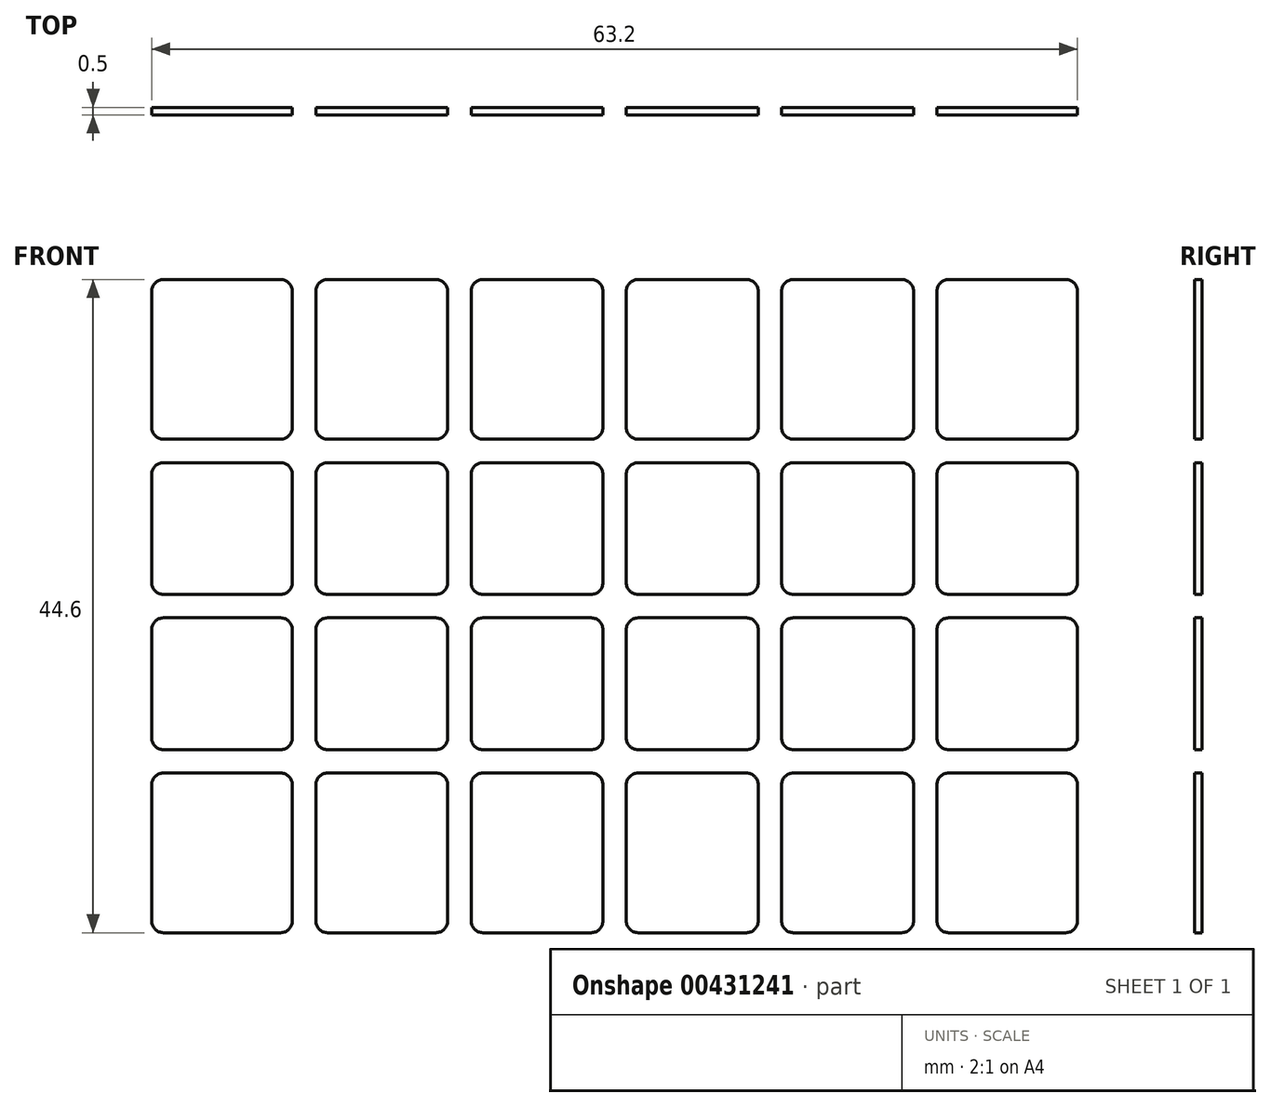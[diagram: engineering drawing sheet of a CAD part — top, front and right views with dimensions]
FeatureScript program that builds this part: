
annotation { "Feature Type Name" : "Feature", "Feature Type Description" : "" }
export const myFeature = defineFeature(function(context is Context, id is Id, definition is map)
    precondition{}
    {
        {
            var Q0;
            Q0=qCreatedBy(makeId("Front.planeOp"),FACE);
            var sketch = newSketch(context, id + "F0", { "sketchPlane" : qUnion([Q0])});
            skLineSegment(sketch, "E0.bottom", {"start": v(0.8, 0) * mm, "end": v(8.8, 0) * mm});
            skLineSegment(sketch, "E0.top", {"start": v(0.8, 9) * mm, "end": v(8.8, 9) * mm});
            skLineSegment(sketch, "E0.left", {"start": v(0, 0.8) * mm, "end": v(0, 8.2) * mm});
            skLineSegment(sketch, "E0.right", {"start": v(9.6, 0.8) * mm, "end": v(9.6, 8.2) * mm});
            skPoint(sketch, "E1.visualSharp", {"position": v(0, 9) * mm});
            skArc(sketch, "E1.filletArc", {"start": v(0.8, 9) * mm, "mid": v(0.23, 8.77) * mm, "end": v(0, 8.2) * mm});
            skPoint(sketch, "E2.visualSharp", {"position": v(9.6, 9) * mm});
            skArc(sketch, "E2.filletArc", {"start": v(9.6, 8.2) * mm, "mid": v(9.37, 8.77) * mm, "end": v(8.8, 9) * mm});
            skPoint(sketch, "E3.visualSharp", {"position": v(9.6, 0) * mm});
            skArc(sketch, "E3.filletArc", {"start": v(8.8, 0) * mm, "mid": v(9.37, 0.23) * mm, "end": v(9.6, 0.8) * mm});
            skPoint(sketch, "E4.visualSharp", {"position": v(0, 0) * mm});
            skArc(sketch, "E4.filletArc", {"start": v(0, 0.8) * mm, "mid": v(0.23, 0.23) * mm, "end": v(0.8, 0) * mm});
            skLineSegment(sketch, "E5.bottom", {"start": v(12, 0) * mm, "end": v(19.4, 0) * mm});
            skLineSegment(sketch, "E5.top", {"start": v(12, 9) * mm, "end": v(19.4, 9) * mm});
            skLineSegment(sketch, "E5.left", {"start": v(11.2, 0.8) * mm, "end": v(11.2, 8.2) * mm});
            skLineSegment(sketch, "E5.right", {"start": v(20.2, 0.8) * mm, "end": v(20.2, 8.2) * mm});
            skPoint(sketch, "E6.visualSharp", {"position": v(11.2, 9) * mm});
            skArc(sketch, "E6.filletArc", {"start": v(12, 9) * mm, "mid": v(11.43, 8.77) * mm, "end": v(11.2, 8.2) * mm});
            skPoint(sketch, "E7.visualSharp", {"position": v(20.2, 9) * mm});
            skArc(sketch, "E7.filletArc", {"start": v(20.2, 8.2) * mm, "mid": v(19.97, 8.77) * mm, "end": v(19.4, 9) * mm});
            skPoint(sketch, "E8.visualSharp", {"position": v(20.2, 0) * mm});
            skArc(sketch, "E8.filletArc", {"start": v(19.4, 0) * mm, "mid": v(19.97, 0.23) * mm, "end": v(20.2, 0.8) * mm});
            skPoint(sketch, "E9.visualSharp", {"position": v(11.2, 0) * mm});
            skArc(sketch, "E9.filletArc", {"start": v(11.2, 0.8) * mm, "mid": v(11.43, 0.23) * mm, "end": v(12, 0) * mm});
            skLineSegment(sketch, "E10.1.0.0", {"start": v(22.6, 9) * mm, "end": v(30, 9) * mm});
            skLineSegment(sketch, "E10.1.0.1", {"start": v(22.6, 0) * mm, "end": v(30, 0) * mm});
            skLineSegment(sketch, "E10.1.0.2", {"start": v(21.8, 0.8) * mm, "end": v(21.8, 8.2) * mm});
            skPoint(sketch, "E10.1.0.3", {"position": v(21.8, 9) * mm});
            skPoint(sketch, "E10.1.0.4", {"position": v(30.8, 9) * mm});
            skLineSegment(sketch, "E10.1.0.5", {"start": v(30.8, 0.8) * mm, "end": v(30.8, 8.2) * mm});
            skPoint(sketch, "E10.1.0.6", {"position": v(21.8, 0) * mm});
            skPoint(sketch, "E10.1.0.7", {"position": v(30.8, 0) * mm});
            skArc(sketch, "E10.1.0.8", {"start": v(30.8, 8.2) * mm, "mid": v(30.57, 8.77) * mm, "end": v(30, 9) * mm});
            skArc(sketch, "E10.1.0.9", {"start": v(21.8, 0.8) * mm, "mid": v(22.03, 0.23) * mm, "end": v(22.6, 0) * mm});
            skArc(sketch, "E10.1.0.10", {"start": v(30, 0) * mm, "mid": v(30.57, 0.23) * mm, "end": v(30.8, 0.8) * mm});
            skArc(sketch, "E10.1.0.11", {"start": v(22.6, 9) * mm, "mid": v(22.03, 8.77) * mm, "end": v(21.8, 8.2) * mm});
            skLineSegment(sketch, "E10.2.0.0", {"start": v(33.2, 9) * mm, "end": v(40.6, 9) * mm});
            skLineSegment(sketch, "E10.2.0.1", {"start": v(33.2, 0) * mm, "end": v(40.6, 0) * mm});
            skLineSegment(sketch, "E10.2.0.2", {"start": v(32.4, 0.8) * mm, "end": v(32.4, 8.2) * mm});
            skPoint(sketch, "E10.2.0.3", {"position": v(32.4, 9) * mm});
            skPoint(sketch, "E10.2.0.4", {"position": v(41.4, 9) * mm});
            skLineSegment(sketch, "E10.2.0.5", {"start": v(41.4, 0.8) * mm, "end": v(41.4, 8.2) * mm});
            skPoint(sketch, "E10.2.0.6", {"position": v(32.4, 0) * mm});
            skPoint(sketch, "E10.2.0.7", {"position": v(41.4, 0) * mm});
            skArc(sketch, "E10.2.0.8", {"start": v(41.4, 8.2) * mm, "mid": v(41.17, 8.77) * mm, "end": v(40.6, 9) * mm});
            skArc(sketch, "E10.2.0.9", {"start": v(32.4, 0.8) * mm, "mid": v(32.63, 0.23) * mm, "end": v(33.2, 0) * mm});
            skArc(sketch, "E10.2.0.10", {"start": v(40.6, 0) * mm, "mid": v(41.17, 0.23) * mm, "end": v(41.4, 0.8) * mm});
            skArc(sketch, "E10.2.0.11", {"start": v(33.2, 9) * mm, "mid": v(32.63, 8.77) * mm, "end": v(32.4, 8.2) * mm});
            skLineSegment(sketch, "E10.3.0.0", {"start": v(43.8, 9) * mm, "end": v(51.2, 9) * mm});
            skLineSegment(sketch, "E10.3.0.1", {"start": v(43.8, 0) * mm, "end": v(51.2, 0) * mm});
            skLineSegment(sketch, "E10.3.0.2", {"start": v(43, 0.8) * mm, "end": v(43, 8.2) * mm});
            skPoint(sketch, "E10.3.0.3", {"position": v(43, 9) * mm});
            skPoint(sketch, "E10.3.0.4", {"position": v(52, 9) * mm});
            skLineSegment(sketch, "E10.3.0.5", {"start": v(52, 0.8) * mm, "end": v(52, 8.2) * mm});
            skPoint(sketch, "E10.3.0.6", {"position": v(43, 0) * mm});
            skPoint(sketch, "E10.3.0.7", {"position": v(52, 0) * mm});
            skArc(sketch, "E10.3.0.8", {"start": v(52, 8.2) * mm, "mid": v(51.77, 8.77) * mm, "end": v(51.2, 9) * mm});
            skArc(sketch, "E10.3.0.9", {"start": v(43, 0.8) * mm, "mid": v(43.23, 0.23) * mm, "end": v(43.8, 0) * mm});
            skArc(sketch, "E10.3.0.10", {"start": v(51.2, 0) * mm, "mid": v(51.77, 0.23) * mm, "end": v(52, 0.8) * mm});
            skArc(sketch, "E10.3.0.11", {"start": v(43.8, 9) * mm, "mid": v(43.23, 8.77) * mm, "end": v(43, 8.2) * mm});
            skLineSegment(sketch, "E10.direction1", {"start": v(11.2, 0) * mm, "end": v(21.8, 0) * mm, "construction": true});
            skLineSegment(sketch, "E11", {"start": v(30.8, 9) * mm, "end": v(32.4, 9) * mm, "construction": true});
            skLineSegment(sketch, "E12", {"start": v(30.8, 0) * mm, "end": v(32.4, 0) * mm, "construction": true});
            skLineSegment(sketch, "E13", {"start": v(31.6, 9) * mm, "end": v(31.6, 0) * mm, "construction": true});
            skArc(sketch, "E14.MirrorCS", {"start": v(54.4, 0) * mm, "mid": v(53.83, 0.23) * mm, "end": v(53.6, 0.8) * mm});
            skArc(sketch, "E15.MirrorCS", {"start": v(62.4, 9) * mm, "mid": v(62.97, 8.77) * mm, "end": v(63.2, 8.2) * mm});
            skArc(sketch, "E16.MirrorCS", {"start": v(63.2, 0.8) * mm, "mid": v(62.97, 0.23) * mm, "end": v(62.4, 0) * mm});
            skArc(sketch, "E17.MirrorCS", {"start": v(53.6, 8.2) * mm, "mid": v(53.83, 8.77) * mm, "end": v(54.4, 9) * mm});
            skLineSegment(sketch, "E18.MirrorCS", {"start": v(62.4, 9) * mm, "end": v(54.4, 9) * mm});
            skLineSegment(sketch, "E19.MirrorCS", {"start": v(63.2, 0.8) * mm, "end": v(63.2, 8.2) * mm});
            skPoint(sketch, "E20.MirrorP", {"position": v(53.6, 9) * mm});
            skLineSegment(sketch, "E21.MirrorCS", {"start": v(62.4, 0) * mm, "end": v(54.4, 0) * mm});
            skPoint(sketch, "E22.MirrorP", {"position": v(63.2, 9) * mm});
            skLineSegment(sketch, "E23.MirrorCS", {"start": v(53.6, 0.8) * mm, "end": v(53.6, 8.2) * mm});
            skPoint(sketch, "E24.MirrorP", {"position": v(63.2, 0) * mm});
            skPoint(sketch, "E25.MirrorP", {"position": v(53.6, 0) * mm});
            skLineSegment(sketch, "E26", {"start": v(14.28, 9.8) * mm, "end": v(38.56, 9.8) * mm, "construction": true});
            skArc(sketch, "E27.MirrorCS", {"start": v(33.2, 10.6) * mm, "mid": v(32.63, 10.83) * mm, "end": v(32.4, 11.4) * mm});
            skArc(sketch, "E28.MirrorCS", {"start": v(20.2, 11.4) * mm, "mid": v(19.97, 10.83) * mm, "end": v(19.4, 10.6) * mm});
            skArc(sketch, "E29.MirrorCS", {"start": v(52, 11.4) * mm, "mid": v(51.77, 10.83) * mm, "end": v(51.2, 10.6) * mm});
            skArc(sketch, "E30.MirrorCS", {"start": v(19.4, 19.6) * mm, "mid": v(19.97, 19.37) * mm, "end": v(20.2, 18.8) * mm});
            skArc(sketch, "E31.MirrorCS", {"start": v(41.4, 11.4) * mm, "mid": v(41.17, 10.83) * mm, "end": v(40.6, 10.6) * mm});
            skArc(sketch, "E32.MirrorCS", {"start": v(0, 18.8) * mm, "mid": v(0.23, 19.37) * mm, "end": v(0.8, 19.6) * mm});
            skArc(sketch, "E33.MirrorCS", {"start": v(40.6, 19.6) * mm, "mid": v(41.17, 19.37) * mm, "end": v(41.4, 18.8) * mm});
            skArc(sketch, "E34.MirrorCS", {"start": v(43.8, 10.6) * mm, "mid": v(43.23, 10.83) * mm, "end": v(43, 11.4) * mm});
            skArc(sketch, "E35.MirrorCS", {"start": v(12, 10.6) * mm, "mid": v(11.43, 10.83) * mm, "end": v(11.2, 11.4) * mm});
            skArc(sketch, "E36.MirrorCS", {"start": v(53.6, 11.4) * mm, "mid": v(53.83, 10.83) * mm, "end": v(54.4, 10.6) * mm});
            skArc(sketch, "E37.MirrorCS", {"start": v(51.2, 19.6) * mm, "mid": v(51.77, 19.37) * mm, "end": v(52, 18.8) * mm});
            skArc(sketch, "E38.MirrorCS", {"start": v(21.8, 18.8) * mm, "mid": v(22.03, 19.37) * mm, "end": v(22.6, 19.6) * mm});
            skLineSegment(sketch, "E39.MirrorCS", {"start": v(30.8, 19.6) * mm, "end": v(32.4, 19.6) * mm, "construction": true});
            skArc(sketch, "E40.MirrorCS", {"start": v(30.8, 11.4) * mm, "mid": v(30.57, 10.83) * mm, "end": v(30, 10.6) * mm});
            skArc(sketch, "E41.MirrorCS", {"start": v(30, 19.6) * mm, "mid": v(30.57, 19.37) * mm, "end": v(30.8, 18.8) * mm});
            skArc(sketch, "E42.MirrorCS", {"start": v(32.4, 18.8) * mm, "mid": v(32.63, 19.37) * mm, "end": v(33.2, 19.6) * mm});
            skArc(sketch, "E43.MirrorCS", {"start": v(11.2, 18.8) * mm, "mid": v(11.43, 19.37) * mm, "end": v(12, 19.6) * mm});
            skArc(sketch, "E44.MirrorCS", {"start": v(8.8, 19.6) * mm, "mid": v(9.37, 19.37) * mm, "end": v(9.6, 18.8) * mm});
            skArc(sketch, "E45.MirrorCS", {"start": v(43, 18.8) * mm, "mid": v(43.23, 19.37) * mm, "end": v(43.8, 19.6) * mm});
            skArc(sketch, "E46.MirrorCS", {"start": v(22.6, 10.6) * mm, "mid": v(22.03, 10.83) * mm, "end": v(21.8, 11.4) * mm});
            skLineSegment(sketch, "E47.MirrorCS", {"start": v(30.8, 10.6) * mm, "end": v(32.4, 10.6) * mm, "construction": true});
            skArc(sketch, "E48.MirrorCS", {"start": v(54.4, 19.6) * mm, "mid": v(53.83, 19.37) * mm, "end": v(53.6, 18.8) * mm});
            skArc(sketch, "E49.MirrorCS", {"start": v(63.2, 18.8) * mm, "mid": v(62.97, 19.37) * mm, "end": v(62.4, 19.6) * mm});
            skArc(sketch, "E50.MirrorCS", {"start": v(62.4, 10.6) * mm, "mid": v(62.97, 10.83) * mm, "end": v(63.2, 11.4) * mm});
            skArc(sketch, "E51.MirrorCS", {"start": v(0.8, 10.6) * mm, "mid": v(0.23, 10.83) * mm, "end": v(0, 11.4) * mm});
            skArc(sketch, "E52.MirrorCS", {"start": v(9.6, 11.4) * mm, "mid": v(9.37, 10.83) * mm, "end": v(8.8, 10.6) * mm});
            skLineSegment(sketch, "E53.MirrorCS", {"start": v(12, 19.6) * mm, "end": v(19.4, 19.6) * mm});
            skPoint(sketch, "E54.MirrorP", {"position": v(21.8, 10.6) * mm});
            skPoint(sketch, "E55.MirrorP", {"position": v(63.2, 19.6) * mm});
            skLineSegment(sketch, "E56.MirrorCS", {"start": v(62.4, 10.6) * mm, "end": v(54.4, 10.6) * mm});
            skPoint(sketch, "E57.MirrorP", {"position": v(32.4, 10.6) * mm});
            skLineSegment(sketch, "E58.MirrorCS", {"start": v(22.6, 19.6) * mm, "end": v(30, 19.6) * mm});
            skLineSegment(sketch, "E59.MirrorCS", {"start": v(31.6, 10.6) * mm, "end": v(31.6, 19.6) * mm, "construction": true});
            skLineSegment(sketch, "E60.MirrorCS", {"start": v(33.2, 10.6) * mm, "end": v(40.6, 10.6) * mm});
            skPoint(sketch, "E61.MirrorP", {"position": v(20.2, 10.6) * mm});
            skPoint(sketch, "E62.MirrorP", {"position": v(52, 10.6) * mm});
            skPoint(sketch, "E63.MirrorP", {"position": v(43, 19.6) * mm});
            skPoint(sketch, "E64.MirrorP", {"position": v(30.8, 10.6) * mm});
            skLineSegment(sketch, "E65.MirrorCS", {"start": v(52, 18.8) * mm, "end": v(52, 11.4) * mm});
            skLineSegment(sketch, "E66.MirrorCS", {"start": v(11.2, 19.6) * mm, "end": v(21.8, 19.6) * mm, "construction": true});
            skLineSegment(sketch, "E67.MirrorCS", {"start": v(41.4, 18.8) * mm, "end": v(41.4, 11.4) * mm});
            skPoint(sketch, "E68.MirrorP", {"position": v(41.4, 19.6) * mm});
            skPoint(sketch, "E69.MirrorP", {"position": v(53.6, 10.6) * mm});
            skLineSegment(sketch, "E70.MirrorCS", {"start": v(21.8, 18.8) * mm, "end": v(21.8, 11.4) * mm});
            skPoint(sketch, "E71.MirrorP", {"position": v(21.8, 19.6) * mm});
            skLineSegment(sketch, "E72.MirrorCS", {"start": v(62.4, 19.6) * mm, "end": v(54.4, 19.6) * mm});
            skLineSegment(sketch, "E73.MirrorCS", {"start": v(43.8, 10.6) * mm, "end": v(51.2, 10.6) * mm});
            skPoint(sketch, "E74.MirrorP", {"position": v(0, 19.6) * mm});
            skPoint(sketch, "E75.MirrorP", {"position": v(9.6, 19.6) * mm});
            skPoint(sketch, "E76.MirrorP", {"position": v(20.2, 19.6) * mm});
            skPoint(sketch, "E77.MirrorP", {"position": v(32.4, 19.6) * mm});
            skLineSegment(sketch, "E78.MirrorCS", {"start": v(33.2, 19.6) * mm, "end": v(40.6, 19.6) * mm});
            skPoint(sketch, "E79.MirrorP", {"position": v(63.2, 10.6) * mm});
            skLineSegment(sketch, "E80.MirrorCS", {"start": v(22.6, 10.6) * mm, "end": v(30, 10.6) * mm});
            skLineSegment(sketch, "E81.MirrorCS", {"start": v(12, 10.6) * mm, "end": v(19.4, 10.6) * mm});
            skLineSegment(sketch, "E82.MirrorCS", {"start": v(30.8, 18.8) * mm, "end": v(30.8, 11.4) * mm});
            skLineSegment(sketch, "E83.MirrorCS", {"start": v(20.2, 18.8) * mm, "end": v(20.2, 11.4) * mm});
            skPoint(sketch, "E84.MirrorP", {"position": v(53.6, 19.6) * mm});
            skLineSegment(sketch, "E85.MirrorCS", {"start": v(43.8, 19.6) * mm, "end": v(51.2, 19.6) * mm});
            skPoint(sketch, "E86.MirrorP", {"position": v(11.2, 19.6) * mm});
            skLineSegment(sketch, "E87.MirrorCS", {"start": v(43, 18.8) * mm, "end": v(43, 11.4) * mm});
            skLineSegment(sketch, "E88.MirrorCS", {"start": v(53.6, 18.8) * mm, "end": v(53.6, 11.4) * mm});
            skPoint(sketch, "E89.MirrorP", {"position": v(11.2, 10.6) * mm});
            skLineSegment(sketch, "E90.MirrorCS", {"start": v(11.2, 18.8) * mm, "end": v(11.2, 11.4) * mm});
            skLineSegment(sketch, "E91.MirrorCS", {"start": v(63.2, 18.8) * mm, "end": v(63.2, 11.4) * mm});
            skPoint(sketch, "E92.MirrorP", {"position": v(0, 10.6) * mm});
            skPoint(sketch, "E93.MirrorP", {"position": v(30.8, 19.6) * mm});
            skPoint(sketch, "E94.MirrorP", {"position": v(52, 19.6) * mm});
            skPoint(sketch, "E95.MirrorP", {"position": v(43, 10.6) * mm});
            skLineSegment(sketch, "E96.MirrorCS", {"start": v(32.4, 18.8) * mm, "end": v(32.4, 11.4) * mm});
            skPoint(sketch, "E97.MirrorP", {"position": v(41.4, 10.6) * mm});
            skLineSegment(sketch, "E98.MirrorCS", {"start": v(0.8, 19.6) * mm, "end": v(8.8, 19.6) * mm});
            skLineSegment(sketch, "E99.MirrorCS", {"start": v(9.6, 18.8) * mm, "end": v(9.6, 11.4) * mm});
            skPoint(sketch, "E100.MirrorP", {"position": v(9.6, 10.6) * mm});
            skLineSegment(sketch, "E101.MirrorCS", {"start": v(0.8, 10.6) * mm, "end": v(8.8, 10.6) * mm});
            skLineSegment(sketch, "E102.MirrorCS", {"start": v(0, 18.8) * mm, "end": v(0, 11.4) * mm});
            skLineSegment(sketch, "E103.bottom", {"start": v(8.8, 21.2) * mm, "end": v(0.8, 21.2) * mm});
            skLineSegment(sketch, "E103.top", {"start": v(8.8, 32.1) * mm, "end": v(0.8, 32.1) * mm});
            skLineSegment(sketch, "E103.left", {"start": v(9.6, 22) * mm, "end": v(9.6, 31.3) * mm});
            skLineSegment(sketch, "E103.right", {"start": v(0, 22) * mm, "end": v(0, 31.3) * mm});
            skPoint(sketch, "E104.visualSharp", {"position": v(0, 32.1) * mm});
            skArc(sketch, "E104.filletArc", {"start": v(0.8, 32.1) * mm, "mid": v(0.23, 31.87) * mm, "end": v(0, 31.3) * mm});
            skPoint(sketch, "E105.visualSharp", {"position": v(9.6, 32.1) * mm});
            skArc(sketch, "E105.filletArc", {"start": v(9.6, 31.3) * mm, "mid": v(9.37, 31.87) * mm, "end": v(8.8, 32.1) * mm});
            skPoint(sketch, "E106.visualSharp", {"position": v(9.6, 21.2) * mm});
            skArc(sketch, "E106.filletArc", {"start": v(8.8, 21.2) * mm, "mid": v(9.37, 21.43) * mm, "end": v(9.6, 22) * mm});
            skPoint(sketch, "E107.visualSharp", {"position": v(0, 21.2) * mm});
            skArc(sketch, "E107.filletArc", {"start": v(0, 22) * mm, "mid": v(0.23, 21.43) * mm, "end": v(0.8, 21.2) * mm});
            skLineSegment(sketch, "E108.bottom", {"start": v(12, 21.2) * mm, "end": v(19.4, 21.2) * mm});
            skLineSegment(sketch, "E108.top", {"start": v(12, 32.1) * mm, "end": v(19.4, 32.1) * mm});
            skLineSegment(sketch, "E108.left", {"start": v(11.2, 22) * mm, "end": v(11.2, 31.3) * mm});
            skLineSegment(sketch, "E108.right", {"start": v(20.2, 22) * mm, "end": v(20.2, 31.3) * mm});
            skPoint(sketch, "E109.visualSharp", {"position": v(11.2, 32.1) * mm});
            skArc(sketch, "E109.filletArc", {"start": v(12, 32.1) * mm, "mid": v(11.43, 31.87) * mm, "end": v(11.2, 31.3) * mm});
            skPoint(sketch, "E110.visualSharp", {"position": v(20.2, 32.1) * mm});
            skArc(sketch, "E110.filletArc", {"start": v(20.2, 31.3) * mm, "mid": v(19.97, 31.87) * mm, "end": v(19.4, 32.1) * mm});
            skPoint(sketch, "E111.visualSharp", {"position": v(20.2, 21.2) * mm});
            skArc(sketch, "E111.filletArc", {"start": v(19.4, 21.2) * mm, "mid": v(19.97, 21.43) * mm, "end": v(20.2, 22) * mm});
            skPoint(sketch, "E112.visualSharp", {"position": v(11.2, 21.2) * mm});
            skArc(sketch, "E112.filletArc", {"start": v(11.2, 22) * mm, "mid": v(11.43, 21.43) * mm, "end": v(12, 21.2) * mm});
            skPoint(sketch, "E113.1.0.0", {"position": v(21.8, 21.2) * mm});
            skPoint(sketch, "E113.1.0.1", {"position": v(21.8, 32.1) * mm});
            skLineSegment(sketch, "E113.1.0.2", {"start": v(21.8, 22) * mm, "end": v(21.8, 31.3) * mm});
            skLineSegment(sketch, "E113.1.0.3", {"start": v(30.8, 22) * mm, "end": v(30.8, 31.3) * mm});
            skPoint(sketch, "E113.1.0.4", {"position": v(30.8, 32.1) * mm});
            skPoint(sketch, "E113.1.0.5", {"position": v(30.8, 21.2) * mm});
            skLineSegment(sketch, "E113.1.0.6", {"start": v(22.6, 21.2) * mm, "end": v(30, 21.2) * mm});
            skLineSegment(sketch, "E113.1.0.7", {"start": v(22.6, 32.1) * mm, "end": v(30, 32.1) * mm});
            skArc(sketch, "E113.1.0.8", {"start": v(30.8, 31.3) * mm, "mid": v(30.57, 31.87) * mm, "end": v(30, 32.1) * mm});
            skArc(sketch, "E113.1.0.9", {"start": v(22.6, 32.1) * mm, "mid": v(22.03, 31.87) * mm, "end": v(21.8, 31.3) * mm});
            skArc(sketch, "E113.1.0.10", {"start": v(30, 21.2) * mm, "mid": v(30.57, 21.43) * mm, "end": v(30.8, 22) * mm});
            skArc(sketch, "E113.1.0.11", {"start": v(21.8, 22) * mm, "mid": v(22.03, 21.43) * mm, "end": v(22.6, 21.2) * mm});
            skPoint(sketch, "E113.2.0.0", {"position": v(32.4, 21.2) * mm});
            skPoint(sketch, "E113.2.0.1", {"position": v(32.4, 32.1) * mm});
            skLineSegment(sketch, "E113.2.0.2", {"start": v(32.4, 22) * mm, "end": v(32.4, 31.3) * mm});
            skLineSegment(sketch, "E113.2.0.3", {"start": v(41.4, 22) * mm, "end": v(41.4, 31.3) * mm});
            skPoint(sketch, "E113.2.0.4", {"position": v(41.4, 32.1) * mm});
            skPoint(sketch, "E113.2.0.5", {"position": v(41.4, 21.2) * mm});
            skLineSegment(sketch, "E113.2.0.6", {"start": v(33.2, 21.2) * mm, "end": v(40.6, 21.2) * mm});
            skLineSegment(sketch, "E113.2.0.7", {"start": v(33.2, 32.1) * mm, "end": v(40.6, 32.1) * mm});
            skArc(sketch, "E113.2.0.8", {"start": v(41.4, 31.3) * mm, "mid": v(41.17, 31.87) * mm, "end": v(40.6, 32.1) * mm});
            skArc(sketch, "E113.2.0.9", {"start": v(33.2, 32.1) * mm, "mid": v(32.63, 31.87) * mm, "end": v(32.4, 31.3) * mm});
            skArc(sketch, "E113.2.0.10", {"start": v(40.6, 21.2) * mm, "mid": v(41.17, 21.43) * mm, "end": v(41.4, 22) * mm});
            skArc(sketch, "E113.2.0.11", {"start": v(32.4, 22) * mm, "mid": v(32.63, 21.43) * mm, "end": v(33.2, 21.2) * mm});
            skPoint(sketch, "E113.3.0.0", {"position": v(43, 21.2) * mm});
            skPoint(sketch, "E113.3.0.1", {"position": v(43, 32.1) * mm});
            skLineSegment(sketch, "E113.3.0.2", {"start": v(43, 22) * mm, "end": v(43, 31.3) * mm});
            skLineSegment(sketch, "E113.3.0.3", {"start": v(52, 22) * mm, "end": v(52, 31.3) * mm});
            skPoint(sketch, "E113.3.0.4", {"position": v(52, 32.1) * mm});
            skPoint(sketch, "E113.3.0.5", {"position": v(52, 21.2) * mm});
            skLineSegment(sketch, "E113.3.0.6", {"start": v(43.8, 21.2) * mm, "end": v(51.2, 21.2) * mm});
            skLineSegment(sketch, "E113.3.0.7", {"start": v(43.8, 32.1) * mm, "end": v(51.2, 32.1) * mm});
            skArc(sketch, "E113.3.0.8", {"start": v(52, 31.3) * mm, "mid": v(51.77, 31.87) * mm, "end": v(51.2, 32.1) * mm});
            skArc(sketch, "E113.3.0.9", {"start": v(43.8, 32.1) * mm, "mid": v(43.23, 31.87) * mm, "end": v(43, 31.3) * mm});
            skArc(sketch, "E113.3.0.10", {"start": v(51.2, 21.2) * mm, "mid": v(51.77, 21.43) * mm, "end": v(52, 22) * mm});
            skArc(sketch, "E113.3.0.11", {"start": v(43, 22) * mm, "mid": v(43.23, 21.43) * mm, "end": v(43.8, 21.2) * mm});
            skLineSegment(sketch, "E113.direction1", {"start": v(11.2, 21.2) * mm, "end": v(21.8, 21.2) * mm, "construction": true});
            skArc(sketch, "E114.MirrorCS", {"start": v(62.4, 32.1) * mm, "mid": v(62.97, 31.87) * mm, "end": v(63.2, 31.3) * mm});
            skArc(sketch, "E115.MirrorCS", {"start": v(63.2, 22) * mm, "mid": v(62.97, 21.43) * mm, "end": v(62.4, 21.2) * mm});
            skArc(sketch, "E116.MirrorCS", {"start": v(53.6, 31.3) * mm, "mid": v(53.83, 31.87) * mm, "end": v(54.4, 32.1) * mm});
            skArc(sketch, "E117.MirrorCS", {"start": v(54.4, 21.2) * mm, "mid": v(53.83, 21.43) * mm, "end": v(53.6, 22) * mm});
            skLineSegment(sketch, "E118.MirrorCS", {"start": v(54.4, 32.1) * mm, "end": v(62.4, 32.1) * mm});
            skPoint(sketch, "E119.MirrorP", {"position": v(53.6, 32.1) * mm});
            skLineSegment(sketch, "E120.MirrorCS", {"start": v(53.6, 22) * mm, "end": v(53.6, 31.3) * mm});
            skLineSegment(sketch, "E121.MirrorCS", {"start": v(63.2, 22) * mm, "end": v(63.2, 31.3) * mm});
            skLineSegment(sketch, "E122.MirrorCS", {"start": v(54.4, 21.2) * mm, "end": v(62.4, 21.2) * mm});
            skPoint(sketch, "E123.MirrorP", {"position": v(53.6, 21.2) * mm});
            skPoint(sketch, "E124.MirrorP", {"position": v(63.2, 32.1) * mm});
            skPoint(sketch, "E125.MirrorP", {"position": v(63.2, 21.2) * mm});
            skArc(sketch, "E126.MirrorCS", {"start": v(22.6, -12.5) * mm, "mid": v(22.03, -12.27) * mm, "end": v(21.8, -11.7) * mm});
            skArc(sketch, "E127.MirrorCS", {"start": v(19.4, -1.6) * mm, "mid": v(19.97, -1.83) * mm, "end": v(20.2, -2.4) * mm});
            skArc(sketch, "E128.MirrorCS", {"start": v(0, -2.4) * mm, "mid": v(0.23, -1.83) * mm, "end": v(0.8, -1.6) * mm});
            skArc(sketch, "E129.MirrorCS", {"start": v(20.2, -11.7) * mm, "mid": v(19.97, -12.27) * mm, "end": v(19.4, -12.5) * mm});
            skArc(sketch, "E130.MirrorCS", {"start": v(43.8, -12.5) * mm, "mid": v(43.23, -12.27) * mm, "end": v(43, -11.7) * mm});
            skArc(sketch, "E131.MirrorCS", {"start": v(54.4, -1.6) * mm, "mid": v(53.83, -1.83) * mm, "end": v(53.6, -2.4) * mm});
            skArc(sketch, "E132.MirrorCS", {"start": v(30, -1.6) * mm, "mid": v(30.57, -1.83) * mm, "end": v(30.8, -2.4) * mm});
            skArc(sketch, "E133.MirrorCS", {"start": v(21.8, -2.4) * mm, "mid": v(22.03, -1.83) * mm, "end": v(22.6, -1.6) * mm});
            skArc(sketch, "E134.MirrorCS", {"start": v(43, -2.4) * mm, "mid": v(43.23, -1.83) * mm, "end": v(43.8, -1.6) * mm});
            skArc(sketch, "E135.MirrorCS", {"start": v(41.4, -11.7) * mm, "mid": v(41.17, -12.27) * mm, "end": v(40.6, -12.5) * mm});
            skArc(sketch, "E136.MirrorCS", {"start": v(0.8, -12.5) * mm, "mid": v(0.23, -12.27) * mm, "end": v(0, -11.7) * mm});
            skArc(sketch, "E137.MirrorCS", {"start": v(52, -11.7) * mm, "mid": v(51.77, -12.27) * mm, "end": v(51.2, -12.5) * mm});
            skArc(sketch, "E138.MirrorCS", {"start": v(40.6, -1.6) * mm, "mid": v(41.17, -1.83) * mm, "end": v(41.4, -2.4) * mm});
            skArc(sketch, "E139.MirrorCS", {"start": v(51.2, -1.6) * mm, "mid": v(51.77, -1.83) * mm, "end": v(52, -2.4) * mm});
            skArc(sketch, "E140.MirrorCS", {"start": v(62.4, -12.5) * mm, "mid": v(62.97, -12.27) * mm, "end": v(63.2, -11.7) * mm});
            skArc(sketch, "E141.MirrorCS", {"start": v(30.8, -11.7) * mm, "mid": v(30.57, -12.27) * mm, "end": v(30, -12.5) * mm});
            skArc(sketch, "E142.MirrorCS", {"start": v(12, -12.5) * mm, "mid": v(11.43, -12.27) * mm, "end": v(11.2, -11.7) * mm});
            skArc(sketch, "E143.MirrorCS", {"start": v(8.8, -1.6) * mm, "mid": v(9.37, -1.83) * mm, "end": v(9.6, -2.4) * mm});
            skArc(sketch, "E144.MirrorCS", {"start": v(53.6, -11.7) * mm, "mid": v(53.83, -12.27) * mm, "end": v(54.4, -12.5) * mm});
            skArc(sketch, "E145.MirrorCS", {"start": v(33.2, -12.5) * mm, "mid": v(32.63, -12.27) * mm, "end": v(32.4, -11.7) * mm});
            skArc(sketch, "E146.MirrorCS", {"start": v(9.6, -11.7) * mm, "mid": v(9.37, -12.27) * mm, "end": v(8.8, -12.5) * mm});
            skArc(sketch, "E147.MirrorCS", {"start": v(63.2, -2.4) * mm, "mid": v(62.97, -1.83) * mm, "end": v(62.4, -1.6) * mm});
            skArc(sketch, "E148.MirrorCS", {"start": v(11.2, -2.4) * mm, "mid": v(11.43, -1.83) * mm, "end": v(12, -1.6) * mm});
            skArc(sketch, "E149.MirrorCS", {"start": v(32.4, -2.4) * mm, "mid": v(32.63, -1.83) * mm, "end": v(33.2, -1.6) * mm});
            skPoint(sketch, "E150.MirrorP", {"position": v(52, -1.6) * mm});
            skLineSegment(sketch, "E151.MirrorCS", {"start": v(12, -1.6) * mm, "end": v(19.4, -1.6) * mm});
            skPoint(sketch, "E152.MirrorP", {"position": v(52, -12.5) * mm});
            skPoint(sketch, "E153.MirrorP", {"position": v(41.4, -12.5) * mm});
            skLineSegment(sketch, "E154.MirrorCS", {"start": v(8.8, -12.5) * mm, "end": v(0.8, -12.5) * mm});
            skLineSegment(sketch, "E155.MirrorCS", {"start": v(33.2, -1.6) * mm, "end": v(40.6, -1.6) * mm});
            skLineSegment(sketch, "E156.MirrorCS", {"start": v(43.8, -12.5) * mm, "end": v(51.2, -12.5) * mm});
            skPoint(sketch, "E157.MirrorP", {"position": v(20.2, -1.6) * mm});
            skLineSegment(sketch, "E158.MirrorCS", {"start": v(12, -12.5) * mm, "end": v(19.4, -12.5) * mm});
            skPoint(sketch, "E159.MirrorP", {"position": v(53.6, -1.6) * mm});
            skPoint(sketch, "E160.MirrorP", {"position": v(0, -1.6) * mm});
            skLineSegment(sketch, "E161.MirrorCS", {"start": v(30.8, -2.4) * mm, "end": v(30.8, -11.7) * mm});
            skPoint(sketch, "E162.MirrorP", {"position": v(0, -12.5) * mm});
            skLineSegment(sketch, "E163.MirrorCS", {"start": v(33.2, -12.5) * mm, "end": v(40.6, -12.5) * mm});
            skLineSegment(sketch, "E164.MirrorCS", {"start": v(11.2, -2.4) * mm, "end": v(11.2, -11.7) * mm});
            skLineSegment(sketch, "E165.MirrorCS", {"start": v(0, -2.4) * mm, "end": v(0, -11.7) * mm});
            skPoint(sketch, "E166.MirrorP", {"position": v(21.8, -1.6) * mm});
            skLineSegment(sketch, "E167.MirrorCS", {"start": v(20.2, -2.4) * mm, "end": v(20.2, -11.7) * mm});
            skLineSegment(sketch, "E168.MirrorCS", {"start": v(11.2, -1.6) * mm, "end": v(21.8, -1.6) * mm, "construction": true});
            skPoint(sketch, "E169.MirrorP", {"position": v(63.2, -1.6) * mm});
            skPoint(sketch, "E170.MirrorP", {"position": v(21.8, -12.5) * mm});
            skPoint(sketch, "E171.MirrorP", {"position": v(11.2, -12.5) * mm});
            skPoint(sketch, "E172.MirrorP", {"position": v(43, -12.5) * mm});
            skLineSegment(sketch, "E173.MirrorCS", {"start": v(22.6, -12.5) * mm, "end": v(30, -12.5) * mm});
            skLineSegment(sketch, "E174.MirrorCS", {"start": v(54.4, -12.5) * mm, "end": v(62.4, -12.5) * mm});
            skPoint(sketch, "E175.MirrorP", {"position": v(32.4, -12.5) * mm});
            skLineSegment(sketch, "E176.MirrorCS", {"start": v(22.6, -1.6) * mm, "end": v(30, -1.6) * mm});
            skPoint(sketch, "E177.MirrorP", {"position": v(9.6, -12.5) * mm});
            skPoint(sketch, "E178.MirrorP", {"position": v(41.4, -1.6) * mm});
            skLineSegment(sketch, "E179.MirrorCS", {"start": v(52, -2.4) * mm, "end": v(52, -11.7) * mm});
            skLineSegment(sketch, "E180.MirrorCS", {"start": v(43.8, -1.6) * mm, "end": v(51.2, -1.6) * mm});
            skPoint(sketch, "E181.MirrorP", {"position": v(43, -1.6) * mm});
            skPoint(sketch, "E182.MirrorP", {"position": v(9.6, -1.6) * mm});
            skLineSegment(sketch, "E183.MirrorCS", {"start": v(9.6, -2.4) * mm, "end": v(9.6, -11.7) * mm});
            skPoint(sketch, "E184.MirrorP", {"position": v(30.8, -12.5) * mm});
            skPoint(sketch, "E185.MirrorP", {"position": v(63.2, -12.5) * mm});
            skLineSegment(sketch, "E186.MirrorCS", {"start": v(41.4, -2.4) * mm, "end": v(41.4, -11.7) * mm});
            skLineSegment(sketch, "E187.MirrorCS", {"start": v(54.4, -1.6) * mm, "end": v(62.4, -1.6) * mm});
            skPoint(sketch, "E188.MirrorP", {"position": v(53.6, -12.5) * mm});
            skLineSegment(sketch, "E189.MirrorCS", {"start": v(32.4, -2.4) * mm, "end": v(32.4, -11.7) * mm});
            skPoint(sketch, "E190.MirrorP", {"position": v(20.2, -12.5) * mm});
            skPoint(sketch, "E191.MirrorP", {"position": v(30.8, -1.6) * mm});
            skPoint(sketch, "E192.MirrorP", {"position": v(11.2, -1.6) * mm});
            skLineSegment(sketch, "E193.MirrorCS", {"start": v(53.6, -2.4) * mm, "end": v(53.6, -11.7) * mm});
            skPoint(sketch, "E194.MirrorP", {"position": v(32.4, -1.6) * mm});
            skLineSegment(sketch, "E195.MirrorCS", {"start": v(43, -2.4) * mm, "end": v(43, -11.7) * mm});
            skLineSegment(sketch, "E196.MirrorCS", {"start": v(21.8, -2.4) * mm, "end": v(21.8, -11.7) * mm});
            skLineSegment(sketch, "E197.MirrorCS", {"start": v(63.2, -2.4) * mm, "end": v(63.2, -11.7) * mm});
            skLineSegment(sketch, "E198.MirrorCS", {"start": v(8.8, -1.6) * mm, "end": v(0.8, -1.6) * mm});
            skSolve(sketch);
        }
        {
            var Q0;
            Q0=qSketchRegion(id+"F0",true);
            extrude(context, id + "F1", {"entities" : qUnion([Q0]), "depth" : 0.5 * mm});
        }
    });
